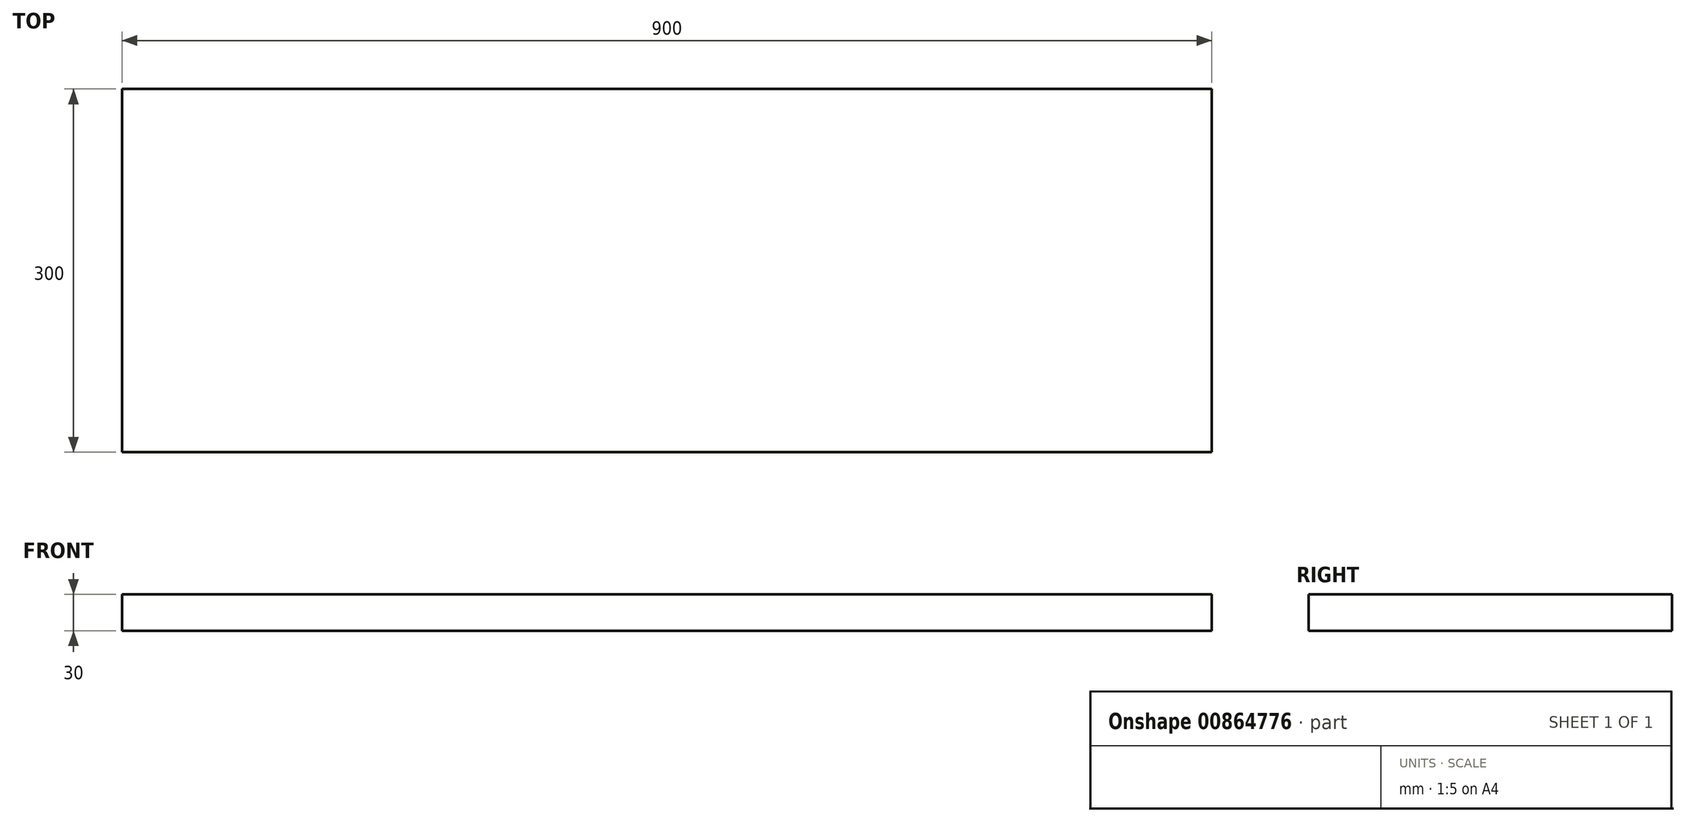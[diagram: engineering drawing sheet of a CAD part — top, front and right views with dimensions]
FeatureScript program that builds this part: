
annotation { "Feature Type Name" : "Feature", "Feature Type Description" : "" }
export const myFeature = defineFeature(function(context is Context, id is Id, definition is map)
    precondition{}
    {
        {
            var Q0;
            Q0=qCreatedBy(makeId("Top.planeOp"),FACE);
            var sketch = newSketch(context, id + "F0", { "sketchPlane" : qUnion([Q0])});
            skLineSegment(sketch, "E0.bottom", {"start": v(0, 0) * mm, "end": v(900, 0) * mm});
            skLineSegment(sketch, "E0.top", {"start": v(0, -300) * mm, "end": v(900, -300) * mm});
            skLineSegment(sketch, "E0.left", {"start": v(0, 0) * mm, "end": v(0, -300) * mm});
            skLineSegment(sketch, "E0.right", {"start": v(900, 0) * mm, "end": v(900, -300) * mm});
            skSolve(sketch);
        }
        {
            var Q0;
            Q0=makeQuery(id+"F0.imprint","IMPRINT",FACE,{"disambiguationData":[TD([[makeQuery(id+"F0.imprint","IMPRINT",EDGE,{"derivedFrom":sQuery(id+"F0.wireOp",EDGE,"E0.bottom")}),-1.0]])]});
            extrude(context, id + "F1", {"entities" : qUnion([Q0]), "depth" : 30 * mm, "offsetDistance" : 25.4 * mm});
        }
    });
